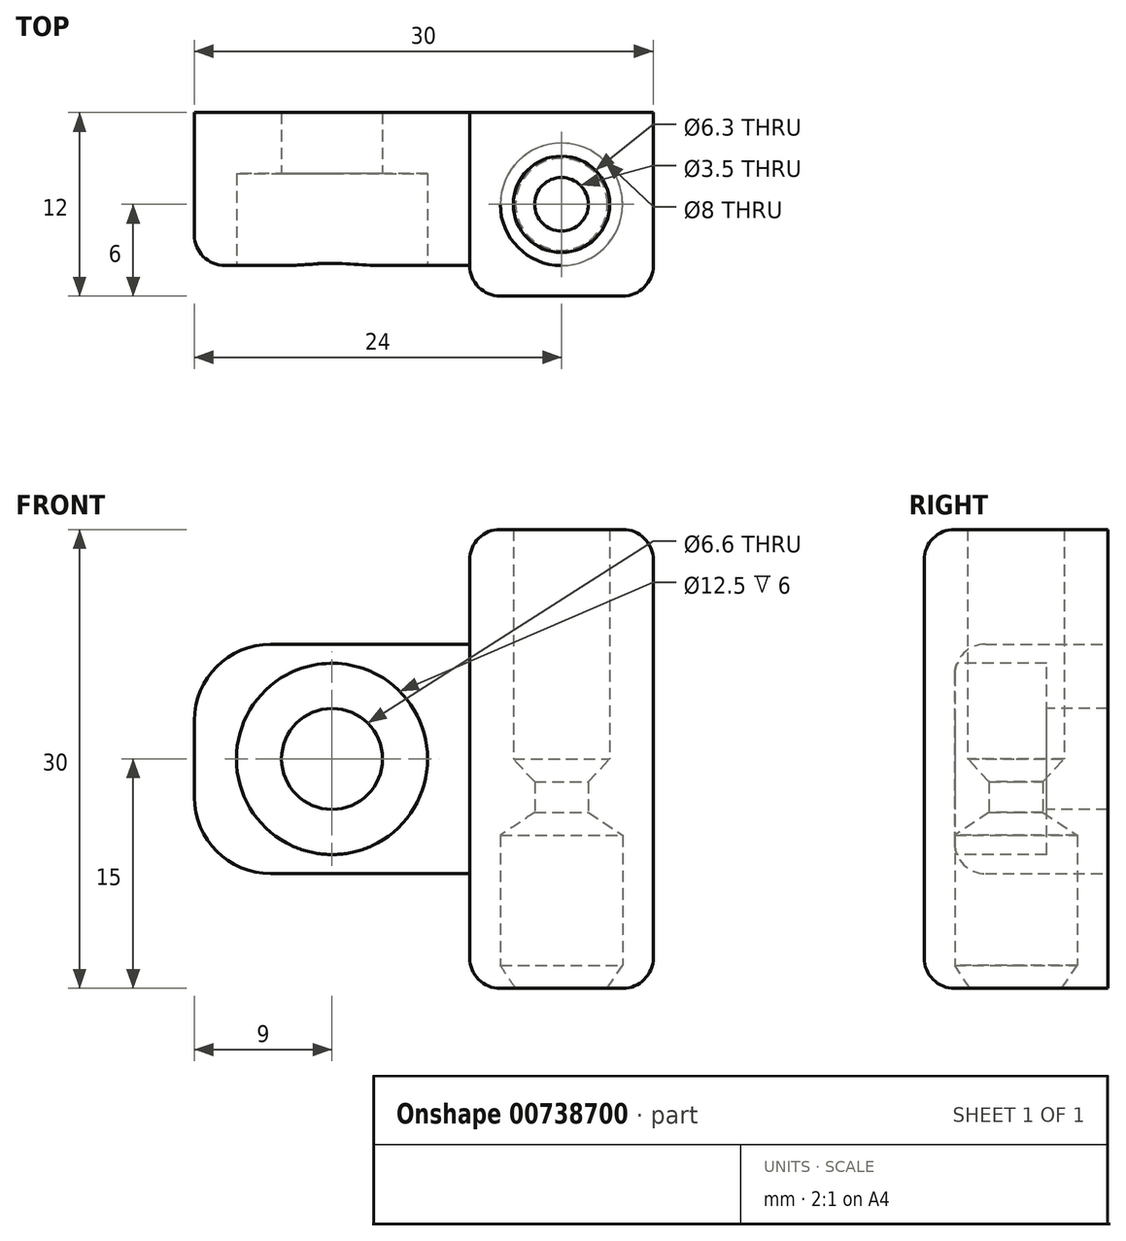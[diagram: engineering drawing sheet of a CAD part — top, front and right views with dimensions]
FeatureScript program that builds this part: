
annotation { "Feature Type Name" : "Feature", "Feature Type Description" : "" }
export const myFeature = defineFeature(function(context is Context, id is Id, definition is map)
    precondition{}
    {
        {
            var Q0;
            Q0=qCreatedBy(makeId("Front.planeOp"),FACE);
            var sketch = newSketch(context, id + "F0", { "sketchPlane" : qUnion([Q0])});
            skLineSegment(sketch, "E0", {"start": v(0, 0) * mm, "end": v(0, 15) * mm});
            skLineSegment(sketch, "E1", {"start": v(0, 15) * mm, "end": v(12, 15) * mm});
            skLineSegment(sketch, "E2", {"start": v(12, 15) * mm, "end": v(12, -15) * mm});
            skLineSegment(sketch, "E3", {"start": v(12, -15) * mm, "end": v(0, -15) * mm});
            skLineSegment(sketch, "E4", {"start": v(0, -15) * mm, "end": v(0, 0) * mm});
            skLineSegment(sketch, "E5", {"start": v(0, 7.5) * mm, "end": v(-18, 7.5) * mm});
            skLineSegment(sketch, "E6", {"start": v(-18, 7.5) * mm, "end": v(-18, -7.5) * mm});
            skLineSegment(sketch, "E7", {"start": v(-18, -7.5) * mm, "end": v(0, -7.5) * mm});
            skSolve(sketch);
        }
        {
            var Q0;
            {var subQ0=sQuery(id+"F0.wireOp",EDGE,"E1");Q0=makeQuery(id+"F0.imprint","IMPRINT",FACE,{"disambiguationData":[TD([[makeQuery(id+"F0.imprint","IMPRINT",EDGE,{"derivedFrom":subQ0}),-1.0]])]});}
            extrude(context, id + "F1", {"entities" : qUnion([Q0]), "depth" : 12 * mm, "offsetDistance" : 25 * mm});
        }
        {
            var Q0;
            {var subQ0=sQuery(id+"F0.wireOp",EDGE,"E5");Q0=makeQuery(id+"F0.imprint","IMPRINT",FACE,{"disambiguationData":[TD([[makeQuery(id+"F0.imprint","IMPRINT",EDGE,{"derivedFrom":subQ0}),1.0]])]});}
            extrude(context, id + "F2", {"entities" : qUnion([Q0]), "operationType" : NewBodyOperationType.ADD, "depth" : 10 * mm, "offsetDistance" : 25 * mm});
        }
        {
            var Q0;
            Q0=makeQuery(id+"F2.opExtrude","CAP_FACE",FACE,{"disambiguationData":[OSD([sQuery(id+"F0.wireOp",EDGE,"E0"),sQuery(id+"F0.wireOp",EDGE,"E4"),sQuery(id+"F0.wireOp",EDGE,"E5"),sQuery(id+"F0.wireOp",EDGE,"E6"),sQuery(id+"F0.wireOp",EDGE,"E7")])],"isStart":false});
            var sketch = newSketch(context, id + "F3", { "sketchPlane" : qUnion([Q0])});
            skPoint(sketch, "E8", {"position": v(-9, 0) * mm});
            skSolve(sketch);
        }
        {
            var Q0;
            Q0=sQuery(id+"F3.wireOp",VERTEX,"E8");
            var Q1;
            Q1=makeQuery(id+"F1.opExtrude","SWEPT_BODY",BODY,{"disambiguationData":[OSD([sQuery(id+"F0.wireOp",EDGE,"E0"),sQuery(id+"F0.wireOp",EDGE,"E1"),sQuery(id+"F0.wireOp",EDGE,"E2"),sQuery(id+"F0.wireOp",EDGE,"E3"),sQuery(id+"F0.wireOp",EDGE,"E4")])]});
            hole(context, id + "F4", {"style" : HoleStyle.C_BORE, "endStyle" : HoleEndStyle.THROUGH, "holeDiameter" : 6.6 * mm, "cBoreDiameter" : 12.5 * mm, "cBoreDepth" : 6 * mm, "majorDiameter" : 5 * mm, "isTappedThrough" : true, "tappedDepth" : 12 * mm, "tapClearance" : 3, "locations" : qUnion([Q0]), "scope" : qUnion([Q1])});
        }
        {
            var Q0;
            Q0=makeQuery(id+"F1.opExtrude","SWEPT_FACE",FACE,{"disambiguationData":[OSD([sQuery(id+"F0.wireOp",EDGE,"E2")])]});
            cPlane(context, id + "F5", {"entities" : qUnion([Q0]), "cplaneType" : CPlaneType.OFFSET, "offset" : 6 * mm, "oppositeDirection" : true, "width" : 150 * mm, "height" : 150 * mm});
        }
        {
            var Q0;
            Q0=qCreatedBy(id+"F5.planeOp",FACE);
            var sketch = newSketch(context, id + "F6", { "sketchPlane" : qUnion([Q0])});
            skLineSegment(sketch, "E9", {"start": v(-9.15, 15) * mm, "end": v(-9.15, 0) * mm});
            skLineSegment(sketch, "E10", {"start": v(-9.15, 0) * mm, "end": v(-6, 0) * mm});
            skLineSegment(sketch, "E11", {"start": v(-6, 0) * mm, "end": v(-6, 15) * mm});
            skLineSegment(sketch, "E12", {"start": v(-9.15, 15) * mm, "end": v(-6, 15) * mm});
            skLineSegment(sketch, "E13", {"start": v(-6, 0) * mm, "end": v(-6, -1.5) * mm});
            skLineSegment(sketch, "E14", {"start": v(-6, -1.5) * mm, "end": v(-7.75, -1.5) * mm});
            skLineSegment(sketch, "E15", {"start": v(-9.15, 0) * mm, "end": v(-7.75, -1.5) * mm});
            skLineSegment(sketch, "E16", {"start": v(-6, -1.5) * mm, "end": v(-6, -3.5) * mm});
            skLineSegment(sketch, "E17", {"start": v(-7.75, -1.5) * mm, "end": v(-7.75, -3.5) * mm});
            skLineSegment(sketch, "E18", {"start": v(-6, -3.5) * mm, "end": v(-6, -5) * mm});
            skLineSegment(sketch, "E19", {"start": v(-6, -5) * mm, "end": v(-6, -15) * mm});
            skLineSegment(sketch, "E20", {"start": v(-6, -5) * mm, "end": v(-10, -5) * mm});
            skLineSegment(sketch, "E21", {"start": v(-10, -5) * mm, "end": v(-10, -13.5) * mm});
            skLineSegment(sketch, "E22", {"start": v(-7.75, -3.5) * mm, "end": v(-10, -5) * mm});
            skLineSegment(sketch, "E23", {"start": v(-6, -15) * mm, "end": v(-9, -15) * mm});
            skLineSegment(sketch, "E24", {"start": v(-9, -15) * mm, "end": v(-10, -13.5) * mm});
            skSolve(sketch);
        }
        {
            var Q0;
            Q0 = qSketchRegion(id + "F6", true);
            var Q1;
            Q1=sQuery(id+"F6.wireOp",EDGE,"E13");
            revolve(context, id + "F7", {"operationType" : NewBodyOperationType.REMOVE, "surfaceOperationType" : NewSurfaceOperationType.NEW, "entities" : qUnion([Q0]), "axis" : qUnion([Q1]), "revolveType" : RevolveType.FULL, "oppositeDirection" : true});
        }
        {
            var Q0;
            Q0=makeQuery(id+"F2.opExtrude","CAP_EDGE",EDGE,{"disambiguationData":[OSD([sQuery(id+"F0.wireOp",EDGE,"E6")])],"isStart":false});
            var Q1;
            Q1=makeQuery(id+"F2.opExtrude","CAP_EDGE",EDGE,{"disambiguationData":[OSD([sQuery(id+"F0.wireOp",EDGE,"E7")])],"isStart":false});
            var Q2;
            Q2=makeQuery(id+"F2.opExtrude","CAP_EDGE",EDGE,{"disambiguationData":[OSD([sQuery(id+"F0.wireOp",EDGE,"E5")])],"isStart":false});
            var Q3;
            Q3=makeQuery(id+"F1.opExtrude","CAP_EDGE",EDGE,{"disambiguationData":[OSD([sQuery(id+"F0.wireOp",EDGE,"E0"),sQuery(id+"F0.wireOp",EDGE,"E4")])],"isStart":false});
            var Q4;
            Q4=makeQuery(id+"F1.opExtrude","CAP_EDGE",EDGE,{"disambiguationData":[OSD([sQuery(id+"F0.wireOp",EDGE,"E2")])],"isStart":false});
            var Q5;
            Q5=makeQuery(id+"F1.opExtrude","CAP_EDGE",EDGE,{"disambiguationData":[OSD([sQuery(id+"F0.wireOp",EDGE,"E3")])],"isStart":false});
            var Q6;
            Q6=makeQuery(id+"F1.opExtrude","CAP_EDGE",EDGE,{"disambiguationData":[OSD([sQuery(id+"F0.wireOp",EDGE,"E1")])],"isStart":false});
            var Q7;
            Q7=makeQuery(id+"F1.opExtrude","SWEPT_EDGE",EDGE,{"disambiguationData":[OSD([sQuery(id+"F0.wireOp",EDGE,"E0"),sQuery(id+"F0.wireOp",EDGE,"E1")])]});
            var Q8;
            Q8=makeQuery(id+"F1.opExtrude","SWEPT_EDGE",EDGE,{"disambiguationData":[OSD([sQuery(id+"F0.wireOp",EDGE,"E1"),sQuery(id+"F0.wireOp",EDGE,"E2")])]});
            var Q9;
            Q9=makeQuery(id+"F1.opExtrude","SWEPT_EDGE",EDGE,{"disambiguationData":[OSD([sQuery(id+"F0.wireOp",EDGE,"E2"),sQuery(id+"F0.wireOp",EDGE,"E3")])]});
            var Q10;
            Q10=makeQuery(id+"F1.opExtrude","SWEPT_EDGE",EDGE,{"disambiguationData":[OSD([sQuery(id+"F0.wireOp",EDGE,"E3"),sQuery(id+"F0.wireOp",EDGE,"E4")])]});
            fillet(context, id + "F8", {"entities" : qUnion([Q0, Q1, Q2, Q3, Q4, Q5, Q6, Q7, Q8, Q9, Q10]), "radius" : 2 * mm, "tangentPropagation" : true, "allowEdgeOverflow" : false});
        }
        {
            var Q0;
            Q0=makeQuery(id+"F2.opExtrude","SWEPT_EDGE",EDGE,{"disambiguationData":[OSD([sQuery(id+"F0.wireOp",EDGE,"E5"),sQuery(id+"F0.wireOp",EDGE,"E6")])]});
            var Q1;
            Q1=makeQuery(id+"F2.opExtrude","SWEPT_EDGE",EDGE,{"disambiguationData":[OSD([sQuery(id+"F0.wireOp",EDGE,"E6"),sQuery(id+"F0.wireOp",EDGE,"E7")])]});
            var Q2;
            Q2=makeQuery(id+"F2.opExtrude","SWEPT_EDGE",EDGE,{"disambiguationData":[OSD([sQuery(id+"F0.wireOp",EDGE,"E4"),sQuery(id+"F0.wireOp",EDGE,"E7")])]});
            fillet(context, id + "F9", {"entities" : qUnion([Q0, Q1, Q2]), "radius" : 5 * mm, "tangentPropagation" : true, "allowEdgeOverflow" : false});
        }
    });
